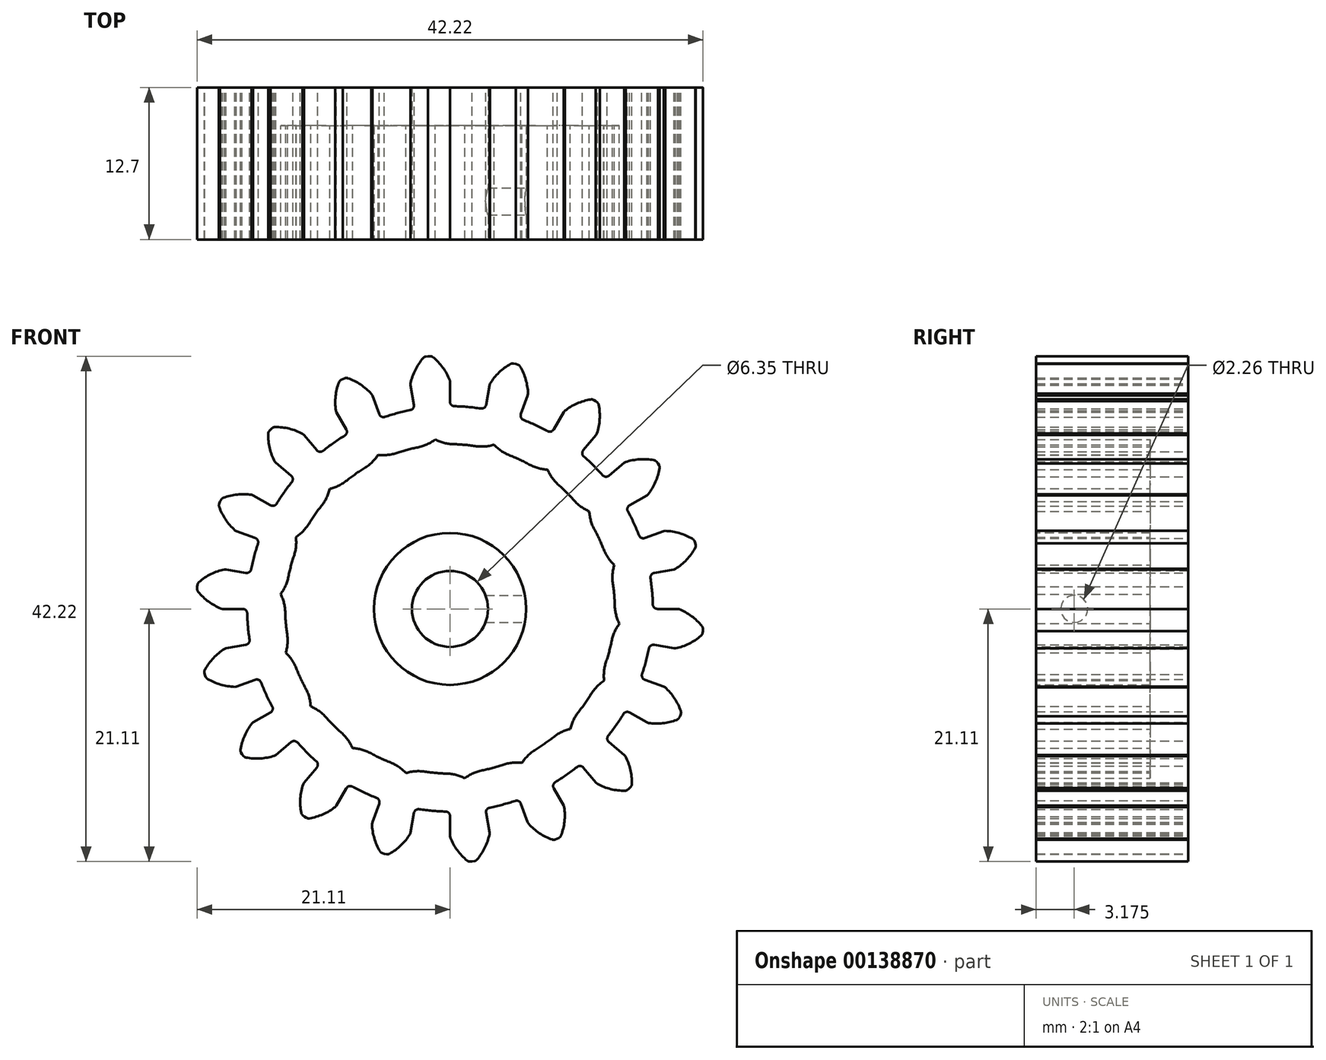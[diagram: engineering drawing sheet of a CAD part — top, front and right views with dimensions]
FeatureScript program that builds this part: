
annotation { "Feature Type Name" : "Feature", "Feature Type Description" : "" }
export const myFeature = defineFeature(function(context is Context, id is Id, definition is map)
    precondition{}
    {
        {
            var Q0;
            Q0=qCreatedBy(makeId("Front.planeOp"),FACE);
            var sketch = newSketch(context, id + "F0", { "sketchPlane" : qUnion([Q0])});
            skArc(sketch, "E0", {"start": v(-3.3, 16.6) * mm, "mid": v(-4.38, 16.36) * mm, "end": v(-5.44, 16.04) * mm});
            skArc(sketch, "E1.trimOffspring", {"start": v(-0.03, 19.12) * mm, "mid": v(-0.6, 20.16) * mm, "end": v(-1.43, 21.02) * mm});
            skLineSegment(sketch, "E2", {"start": v(-1.67, 21.11) * mm, "end": v(-1.85, 21.11) * mm});
            skLineSegment(sketch, "E3", {"start": v(0, 18.98) * mm, "end": v(0, 17.31) * mm});
            skLineSegment(sketch, "E4.MirrorCS", {"start": v(-2.02, 21.08) * mm, "end": v(-1.85, 21.11) * mm});
            skArc(sketch, "E5.MirrorCS", {"start": v(-3.3, 18.83) * mm, "mid": v(-2.9, 19.96) * mm, "end": v(-2.25, 20.95) * mm});
            skLineSegment(sketch, "E6.MirrorCS", {"start": v(-3.3, 18.69) * mm, "end": v(-3, 17.05) * mm});
            skPoint(sketch, "E7.visualSharp", {"position": v(-3.3, 18.76) * mm});
            skArc(sketch, "E7.filletArc", {"start": v(-3.3, 18.83) * mm, "mid": v(-3.3, 18.76) * mm, "end": v(-3.3, 18.69) * mm});
            skPoint(sketch, "E8.visualSharp", {"position": v(0, 19.05) * mm});
            skArc(sketch, "E8.filletArc", {"start": v(0, 18.98) * mm, "mid": v(0, 19.05) * mm, "end": v(-0.03, 19.12) * mm});
            skPoint(sketch, "E9.visualSharp", {"position": v(-2.94, 16.68) * mm});
            skArc(sketch, "E9.filletArc", {"start": v(-3.3, 16.6) * mm, "mid": v(-3.07, 16.77) * mm, "end": v(-3, 17.05) * mm});
            skPoint(sketch, "E10.visualSharp", {"position": v(0, 16.93) * mm});
            skArc(sketch, "E10.filletArc", {"start": v(0, 17.31) * mm, "mid": v(0.1, 17.04) * mm, "end": v(0.37, 16.93) * mm});
            skPoint(sketch, "E11.visualSharp", {"position": v(-2.15, 21.06) * mm});
            skArc(sketch, "E11.filletArc", {"start": v(-2.02, 21.08) * mm, "mid": v(-2.15, 21.04) * mm, "end": v(-2.25, 20.95) * mm});
            skPoint(sketch, "E12.visualSharp", {"position": v(-1.54, 21.11) * mm});
            skArc(sketch, "E12.filletArc", {"start": v(-1.43, 21.02) * mm, "mid": v(-1.54, 21.09) * mm, "end": v(-1.67, 21.11) * mm});
            skArc(sketch, "E13.1.0", {"start": v(-9.54, 16.57) * mm, "mid": v(-9.55, 17.76) * mm, "end": v(-9.28, 18.92) * mm});
            skLineSegment(sketch, "E13.1.1", {"start": v(-9.49, 16.44) * mm, "end": v(-8.66, 15) * mm});
            skArc(sketch, "E13.1.2", {"start": v(-8.79, 14.47) * mm, "mid": v(-8.62, 14.7) * mm, "end": v(-8.66, 15) * mm});
            skLineSegment(sketch, "E13.1.3", {"start": v(-9.11, 19.12) * mm, "end": v(-8.96, 19.2) * mm});
            skLineSegment(sketch, "E13.1.4", {"start": v(-8.79, 19.27) * mm, "end": v(-8.96, 19.2) * mm});
            skArc(sketch, "E13.1.5", {"start": v(-8.53, 19.27) * mm, "mid": v(-8.66, 19.3) * mm, "end": v(-8.79, 19.27) * mm});
            skArc(sketch, "E13.1.6", {"start": v(-9.11, 19.12) * mm, "mid": v(-9.21, 19.03) * mm, "end": v(-9.28, 18.92) * mm});
            skArc(sketch, "E13.1.7", {"start": v(-6.57, 17.96) * mm, "mid": v(-7.47, 18.74) * mm, "end": v(-8.53, 19.27) * mm});
            skLineSegment(sketch, "E13.1.8", {"start": v(-6.5, 17.83) * mm, "end": v(-5.92, 16.27) * mm});
            skArc(sketch, "E13.1.9", {"start": v(-5.92, 16.27) * mm, "mid": v(-5.73, 16.05) * mm, "end": v(-5.44, 16.04) * mm});
            skPoint(sketch, "E13.1.10", {"position": v(-6.52, 17.9) * mm});
            skPoint(sketch, "E13.1.11", {"position": v(-9.53, 16.5) * mm});
            skArc(sketch, "E13.2.0", {"start": v(-14.63, 12.31) * mm, "mid": v(-15.05, 13.42) * mm, "end": v(-15.19, 14.6) * mm});
            skLineSegment(sketch, "E13.2.1", {"start": v(-14.54, 12.2) * mm, "end": v(-13.26, 11.13) * mm});
            skArc(sketch, "E13.2.2", {"start": v(-13.2, 10.6) * mm, "mid": v(-13.13, 10.87) * mm, "end": v(-13.26, 11.13) * mm});
            skLineSegment(sketch, "E13.2.3", {"start": v(-15.1, 14.85) * mm, "end": v(-14.98, 14.98) * mm});
            skLineSegment(sketch, "E13.2.4", {"start": v(-14.85, 15.1) * mm, "end": v(-14.98, 14.98) * mm});
            skArc(sketch, "E13.2.5", {"start": v(-14.6, 15.19) * mm, "mid": v(-14.74, 15.16) * mm, "end": v(-14.85, 15.1) * mm});
            skArc(sketch, "E13.2.6", {"start": v(-15.1, 14.85) * mm, "mid": v(-15.16, 14.74) * mm, "end": v(-15.19, 14.6) * mm});
            skArc(sketch, "E13.2.7", {"start": v(-12.31, 14.63) * mm, "mid": v(-13.42, 15.05) * mm, "end": v(-14.6, 15.19) * mm});
            skLineSegment(sketch, "E13.2.8", {"start": v(-12.2, 14.54) * mm, "end": v(-11.13, 13.26) * mm});
            skArc(sketch, "E13.2.9", {"start": v(-11.13, 13.26) * mm, "mid": v(-10.87, 13.13) * mm, "end": v(-10.6, 13.2) * mm});
            skPoint(sketch, "E13.2.10", {"position": v(-12.25, 14.6) * mm});
            skPoint(sketch, "E13.2.11", {"position": v(-14.6, 12.25) * mm});
            skArc(sketch, "E13.3.0", {"start": v(-17.96, 6.57) * mm, "mid": v(-18.74, 7.47) * mm, "end": v(-19.27, 8.53) * mm});
            skLineSegment(sketch, "E13.3.1", {"start": v(-17.83, 6.5) * mm, "end": v(-16.27, 5.92) * mm});
            skArc(sketch, "E13.3.2", {"start": v(-16.04, 5.44) * mm, "mid": v(-16.05, 5.73) * mm, "end": v(-16.27, 5.92) * mm});
            skLineSegment(sketch, "E13.3.3", {"start": v(-19.27, 8.79) * mm, "end": v(-19.2, 8.96) * mm});
            skLineSegment(sketch, "E13.3.4", {"start": v(-19.12, 9.11) * mm, "end": v(-19.2, 8.96) * mm});
            skArc(sketch, "E13.3.5", {"start": v(-18.92, 9.28) * mm, "mid": v(-19.03, 9.21) * mm, "end": v(-19.12, 9.11) * mm});
            skArc(sketch, "E13.3.6", {"start": v(-19.27, 8.79) * mm, "mid": v(-19.3, 8.66) * mm, "end": v(-19.27, 8.53) * mm});
            skArc(sketch, "E13.3.7", {"start": v(-16.57, 9.54) * mm, "mid": v(-17.76, 9.55) * mm, "end": v(-18.92, 9.28) * mm});
            skLineSegment(sketch, "E13.3.8", {"start": v(-16.44, 9.49) * mm, "end": v(-15, 8.66) * mm});
            skArc(sketch, "E13.3.9", {"start": v(-15, 8.66) * mm, "mid": v(-14.7, 8.62) * mm, "end": v(-14.47, 8.79) * mm});
            skPoint(sketch, "E13.3.10", {"position": v(-16.5, 9.53) * mm});
            skPoint(sketch, "E13.3.11", {"position": v(-17.9, 6.52) * mm});
            skArc(sketch, "E13.4.0", {"start": v(-19.12, 0.03) * mm, "mid": v(-20.16, 0.6) * mm, "end": v(-21.02, 1.43) * mm});
            skLineSegment(sketch, "E13.4.1", {"start": v(-18.98, 0) * mm, "end": v(-17.31, 0) * mm});
            skArc(sketch, "E13.4.2", {"start": v(-16.93, -0.37) * mm, "mid": v(-17.04, -0.1) * mm, "end": v(-17.31, 0) * mm});
            skLineSegment(sketch, "E13.4.3", {"start": v(-21.11, 1.67) * mm, "end": v(-21.11, 1.85) * mm});
            skLineSegment(sketch, "E13.4.4", {"start": v(-21.08, 2.02) * mm, "end": v(-21.11, 1.85) * mm});
            skArc(sketch, "E13.4.5", {"start": v(-20.95, 2.25) * mm, "mid": v(-21.04, 2.15) * mm, "end": v(-21.08, 2.02) * mm});
            skArc(sketch, "E13.4.6", {"start": v(-21.11, 1.67) * mm, "mid": v(-21.09, 1.54) * mm, "end": v(-21.02, 1.43) * mm});
            skArc(sketch, "E13.4.7", {"start": v(-18.83, 3.3) * mm, "mid": v(-19.96, 2.9) * mm, "end": v(-20.95, 2.25) * mm});
            skLineSegment(sketch, "E13.4.8", {"start": v(-18.69, 3.3) * mm, "end": v(-17.05, 3) * mm});
            skArc(sketch, "E13.4.9", {"start": v(-17.05, 3) * mm, "mid": v(-16.77, 3.07) * mm, "end": v(-16.6, 3.3) * mm});
            skPoint(sketch, "E13.4.10", {"position": v(-18.76, 3.3) * mm});
            skPoint(sketch, "E13.4.11", {"position": v(-19.05, 0) * mm});
            skArc(sketch, "E13.5.0", {"start": v(-17.98, -6.51) * mm, "mid": v(-19.15, -6.32) * mm, "end": v(-20.24, -5.85) * mm});
            skLineSegment(sketch, "E13.5.1", {"start": v(-17.83, -6.5) * mm, "end": v(-16.27, -5.92) * mm});
            skArc(sketch, "E13.5.2", {"start": v(-15.78, -6.14) * mm, "mid": v(-15.98, -5.93) * mm, "end": v(-16.27, -5.92) * mm});
            skLineSegment(sketch, "E13.5.3", {"start": v(-20.4, -5.65) * mm, "end": v(-20.47, -5.48) * mm});
            skLineSegment(sketch, "E13.5.4", {"start": v(-20.5, -5.3) * mm, "end": v(-20.47, -5.48) * mm});
            skArc(sketch, "E13.5.5", {"start": v(-20.46, -5.06) * mm, "mid": v(-20.5, -5.18) * mm, "end": v(-20.5, -5.3) * mm});
            skArc(sketch, "E13.5.6", {"start": v(-20.4, -5.65) * mm, "mid": v(-20.34, -5.77) * mm, "end": v(-20.24, -5.85) * mm});
            skArc(sketch, "E13.5.7", {"start": v(-18.82, -3.35) * mm, "mid": v(-19.75, -4.1) * mm, "end": v(-20.46, -5.06) * mm});
            skLineSegment(sketch, "E13.5.8", {"start": v(-18.69, -3.3) * mm, "end": v(-17.05, -3) * mm});
            skArc(sketch, "E13.5.9", {"start": v(-17.05, -3) * mm, "mid": v(-16.8, -2.85) * mm, "end": v(-16.74, -2.57) * mm});
            skPoint(sketch, "E13.5.10", {"position": v(-18.76, -3.3) * mm});
            skPoint(sketch, "E13.5.11", {"position": v(-17.9, -6.52) * mm});
            skArc(sketch, "E13.6.0", {"start": v(-14.66, -12.27) * mm, "mid": v(-15.83, -12.5) * mm, "end": v(-17.02, -12.42) * mm});
            skLineSegment(sketch, "E13.6.1", {"start": v(-14.54, -12.2) * mm, "end": v(-13.26, -11.13) * mm});
            skArc(sketch, "E13.6.2", {"start": v(-12.73, -11.17) * mm, "mid": v(-12.99, -11.04) * mm, "end": v(-13.26, -11.13) * mm});
            skLineSegment(sketch, "E13.6.3", {"start": v(-17.24, -12.3) * mm, "end": v(-17.36, -12.15) * mm});
            skLineSegment(sketch, "E13.6.4", {"start": v(-17.45, -12) * mm, "end": v(-17.36, -12.15) * mm});
            skArc(sketch, "E13.6.5", {"start": v(-17.5, -11.75) * mm, "mid": v(-17.5, -11.88) * mm, "end": v(-17.45, -12) * mm});
            skArc(sketch, "E13.6.6", {"start": v(-17.24, -12.3) * mm, "mid": v(-17.14, -12.38) * mm, "end": v(-17.02, -12.42) * mm});
            skArc(sketch, "E13.6.7", {"start": v(-16.54, -9.58) * mm, "mid": v(-17.16, -10.6) * mm, "end": v(-17.5, -11.75) * mm});
            skLineSegment(sketch, "E13.6.8", {"start": v(-16.44, -9.49) * mm, "end": v(-15, -8.66) * mm});
            skArc(sketch, "E13.6.9", {"start": v(-15, -8.66) * mm, "mid": v(-14.81, -8.43) * mm, "end": v(-14.85, -8.14) * mm});
            skPoint(sketch, "E13.6.10", {"position": v(-16.5, -9.52) * mm});
            skPoint(sketch, "E13.6.11", {"position": v(-14.6, -12.25) * mm});
            skArc(sketch, "E13.7.0", {"start": v(-9.58, -16.54) * mm, "mid": v(-10.6, -17.16) * mm, "end": v(-11.75, -17.5) * mm});
            skLineSegment(sketch, "E13.7.1", {"start": v(-9.49, -16.44) * mm, "end": v(-8.66, -15) * mm});
            skArc(sketch, "E13.7.2", {"start": v(-8.14, -14.85) * mm, "mid": v(-8.43, -14.81) * mm, "end": v(-8.66, -15) * mm});
            skLineSegment(sketch, "E13.7.3", {"start": v(-12, -17.45) * mm, "end": v(-12.15, -17.36) * mm});
            skLineSegment(sketch, "E13.7.4", {"start": v(-12.3, -17.24) * mm, "end": v(-12.15, -17.36) * mm});
            skArc(sketch, "E13.7.5", {"start": v(-12.42, -17.02) * mm, "mid": v(-12.38, -17.14) * mm, "end": v(-12.3, -17.24) * mm});
            skArc(sketch, "E13.7.6", {"start": v(-12, -17.45) * mm, "mid": v(-11.88, -17.5) * mm, "end": v(-11.75, -17.5) * mm});
            skArc(sketch, "E13.7.7", {"start": v(-12.27, -14.66) * mm, "mid": v(-12.5, -15.83) * mm, "end": v(-12.42, -17.02) * mm});
            skLineSegment(sketch, "E13.7.8", {"start": v(-12.2, -14.54) * mm, "end": v(-11.13, -13.26) * mm});
            skArc(sketch, "E13.7.9", {"start": v(-11.13, -13.26) * mm, "mid": v(-11.04, -12.99) * mm, "end": v(-11.17, -12.73) * mm});
            skPoint(sketch, "E13.7.10", {"position": v(-12.25, -14.6) * mm});
            skPoint(sketch, "E13.7.11", {"position": v(-9.52, -16.5) * mm});
            skArc(sketch, "E13.8.0", {"start": v(-3.35, -18.82) * mm, "mid": v(-4.1, -19.75) * mm, "end": v(-5.06, -20.46) * mm});
            skLineSegment(sketch, "E13.8.1", {"start": v(-3.3, -18.69) * mm, "end": v(-3, -17.05) * mm});
            skArc(sketch, "E13.8.2", {"start": v(-2.57, -16.74) * mm, "mid": v(-2.85, -16.8) * mm, "end": v(-3, -17.05) * mm});
            skLineSegment(sketch, "E13.8.3", {"start": v(-5.3, -20.5) * mm, "end": v(-5.48, -20.47) * mm});
            skLineSegment(sketch, "E13.8.4", {"start": v(-5.65, -20.4) * mm, "end": v(-5.48, -20.47) * mm});
            skArc(sketch, "E13.8.5", {"start": v(-5.85, -20.24) * mm, "mid": v(-5.77, -20.34) * mm, "end": v(-5.65, -20.4) * mm});
            skArc(sketch, "E13.8.6", {"start": v(-5.3, -20.5) * mm, "mid": v(-5.18, -20.5) * mm, "end": v(-5.06, -20.46) * mm});
            skArc(sketch, "E13.8.7", {"start": v(-6.51, -17.98) * mm, "mid": v(-6.32, -19.15) * mm, "end": v(-5.85, -20.24) * mm});
            skLineSegment(sketch, "E13.8.8", {"start": v(-6.5, -17.83) * mm, "end": v(-5.92, -16.27) * mm});
            skArc(sketch, "E13.8.9", {"start": v(-5.92, -16.27) * mm, "mid": v(-5.93, -15.98) * mm, "end": v(-6.14, -15.78) * mm});
            skPoint(sketch, "E13.8.10", {"position": v(-6.52, -17.9) * mm});
            skPoint(sketch, "E13.8.11", {"position": v(-3.3, -18.76) * mm});
            skArc(sketch, "E13.9.0", {"start": v(3.3, -18.83) * mm, "mid": v(2.9, -19.96) * mm, "end": v(2.25, -20.95) * mm});
            skLineSegment(sketch, "E13.9.1", {"start": v(3.3, -18.69) * mm, "end": v(3, -17.05) * mm});
            skArc(sketch, "E13.9.2", {"start": v(3.3, -16.6) * mm, "mid": v(3.07, -16.77) * mm, "end": v(3, -17.05) * mm});
            skLineSegment(sketch, "E13.9.3", {"start": v(2.02, -21.08) * mm, "end": v(1.85, -21.11) * mm});
            skLineSegment(sketch, "E13.9.4", {"start": v(1.67, -21.11) * mm, "end": v(1.85, -21.11) * mm});
            skArc(sketch, "E13.9.5", {"start": v(1.43, -21.02) * mm, "mid": v(1.54, -21.09) * mm, "end": v(1.67, -21.11) * mm});
            skArc(sketch, "E13.9.6", {"start": v(2.02, -21.08) * mm, "mid": v(2.15, -21.04) * mm, "end": v(2.25, -20.95) * mm});
            skArc(sketch, "E13.9.7", {"start": v(0.03, -19.12) * mm, "mid": v(0.6, -20.16) * mm, "end": v(1.43, -21.02) * mm});
            skLineSegment(sketch, "E13.9.8", {"start": v(0, -18.98) * mm, "end": v(0, -17.31) * mm});
            skArc(sketch, "E13.9.9", {"start": v(0, -17.31) * mm, "mid": v(-0.1, -17.04) * mm, "end": v(-0.37, -16.93) * mm});
            skPoint(sketch, "E13.9.10", {"position": v(0, -19.05) * mm});
            skPoint(sketch, "E13.9.11", {"position": v(3.3, -18.76) * mm});
            skArc(sketch, "E13.10.0", {"start": v(9.54, -16.57) * mm, "mid": v(9.55, -17.76) * mm, "end": v(9.28, -18.92) * mm});
            skLineSegment(sketch, "E13.10.1", {"start": v(9.49, -16.44) * mm, "end": v(8.66, -15) * mm});
            skArc(sketch, "E13.10.2", {"start": v(8.79, -14.47) * mm, "mid": v(8.62, -14.7) * mm, "end": v(8.66, -15) * mm});
            skLineSegment(sketch, "E13.10.3", {"start": v(9.11, -19.12) * mm, "end": v(8.96, -19.2) * mm});
            skLineSegment(sketch, "E13.10.4", {"start": v(8.79, -19.27) * mm, "end": v(8.96, -19.2) * mm});
            skArc(sketch, "E13.10.5", {"start": v(8.53, -19.27) * mm, "mid": v(8.66, -19.3) * mm, "end": v(8.79, -19.27) * mm});
            skArc(sketch, "E13.10.6", {"start": v(9.11, -19.12) * mm, "mid": v(9.21, -19.03) * mm, "end": v(9.28, -18.92) * mm});
            skArc(sketch, "E13.10.7", {"start": v(6.57, -17.96) * mm, "mid": v(7.47, -18.74) * mm, "end": v(8.53, -19.27) * mm});
            skLineSegment(sketch, "E13.10.8", {"start": v(6.5, -17.83) * mm, "end": v(5.92, -16.27) * mm});
            skArc(sketch, "E13.10.9", {"start": v(5.92, -16.27) * mm, "mid": v(5.73, -16.05) * mm, "end": v(5.44, -16.04) * mm});
            skPoint(sketch, "E13.10.10", {"position": v(6.52, -17.9) * mm});
            skPoint(sketch, "E13.10.11", {"position": v(9.53, -16.5) * mm});
            skArc(sketch, "E13.11.0", {"start": v(14.63, -12.31) * mm, "mid": v(15.05, -13.42) * mm, "end": v(15.19, -14.6) * mm});
            skLineSegment(sketch, "E13.11.1", {"start": v(14.54, -12.2) * mm, "end": v(13.26, -11.13) * mm});
            skArc(sketch, "E13.11.2", {"start": v(13.2, -10.6) * mm, "mid": v(13.13, -10.87) * mm, "end": v(13.26, -11.13) * mm});
            skLineSegment(sketch, "E13.11.3", {"start": v(15.1, -14.85) * mm, "end": v(14.98, -14.98) * mm});
            skLineSegment(sketch, "E13.11.4", {"start": v(14.85, -15.1) * mm, "end": v(14.98, -14.98) * mm});
            skArc(sketch, "E13.11.5", {"start": v(14.6, -15.19) * mm, "mid": v(14.74, -15.16) * mm, "end": v(14.85, -15.1) * mm});
            skArc(sketch, "E13.11.6", {"start": v(15.1, -14.85) * mm, "mid": v(15.16, -14.74) * mm, "end": v(15.19, -14.6) * mm});
            skArc(sketch, "E13.11.7", {"start": v(12.31, -14.63) * mm, "mid": v(13.42, -15.05) * mm, "end": v(14.6, -15.19) * mm});
            skLineSegment(sketch, "E13.11.8", {"start": v(12.2, -14.54) * mm, "end": v(11.13, -13.26) * mm});
            skArc(sketch, "E13.11.9", {"start": v(11.13, -13.26) * mm, "mid": v(10.87, -13.13) * mm, "end": v(10.6, -13.2) * mm});
            skPoint(sketch, "E13.11.10", {"position": v(12.25, -14.6) * mm});
            skPoint(sketch, "E13.11.11", {"position": v(14.6, -12.25) * mm});
            skArc(sketch, "E13.12.0", {"start": v(17.96, -6.57) * mm, "mid": v(18.74, -7.47) * mm, "end": v(19.27, -8.53) * mm});
            skLineSegment(sketch, "E13.12.1", {"start": v(17.83, -6.5) * mm, "end": v(16.27, -5.92) * mm});
            skArc(sketch, "E13.12.2", {"start": v(16.04, -5.44) * mm, "mid": v(16.05, -5.73) * mm, "end": v(16.27, -5.92) * mm});
            skLineSegment(sketch, "E13.12.3", {"start": v(19.27, -8.79) * mm, "end": v(19.2, -8.96) * mm});
            skLineSegment(sketch, "E13.12.4", {"start": v(19.12, -9.11) * mm, "end": v(19.2, -8.96) * mm});
            skArc(sketch, "E13.12.5", {"start": v(18.92, -9.28) * mm, "mid": v(19.03, -9.21) * mm, "end": v(19.12, -9.11) * mm});
            skArc(sketch, "E13.12.6", {"start": v(19.27, -8.79) * mm, "mid": v(19.3, -8.66) * mm, "end": v(19.27, -8.53) * mm});
            skArc(sketch, "E13.12.7", {"start": v(16.57, -9.54) * mm, "mid": v(17.76, -9.55) * mm, "end": v(18.92, -9.28) * mm});
            skLineSegment(sketch, "E13.12.8", {"start": v(16.44, -9.49) * mm, "end": v(15, -8.66) * mm});
            skArc(sketch, "E13.12.9", {"start": v(15, -8.66) * mm, "mid": v(14.7, -8.62) * mm, "end": v(14.47, -8.79) * mm});
            skPoint(sketch, "E13.12.10", {"position": v(16.5, -9.53) * mm});
            skPoint(sketch, "E13.12.11", {"position": v(17.9, -6.52) * mm});
            skArc(sketch, "E13.13.0", {"start": v(19.12, -0.03) * mm, "mid": v(20.16, -0.6) * mm, "end": v(21.02, -1.43) * mm});
            skLineSegment(sketch, "E13.13.1", {"start": v(18.98, 0) * mm, "end": v(17.31, 0) * mm});
            skArc(sketch, "E13.13.2", {"start": v(16.93, 0.37) * mm, "mid": v(17.04, 0.1) * mm, "end": v(17.31, 0) * mm});
            skLineSegment(sketch, "E13.13.3", {"start": v(21.11, -1.67) * mm, "end": v(21.11, -1.85) * mm});
            skLineSegment(sketch, "E13.13.4", {"start": v(21.08, -2.02) * mm, "end": v(21.11, -1.85) * mm});
            skArc(sketch, "E13.13.5", {"start": v(20.95, -2.25) * mm, "mid": v(21.04, -2.15) * mm, "end": v(21.08, -2.02) * mm});
            skArc(sketch, "E13.13.6", {"start": v(21.11, -1.67) * mm, "mid": v(21.09, -1.54) * mm, "end": v(21.02, -1.43) * mm});
            skArc(sketch, "E13.13.7", {"start": v(18.83, -3.3) * mm, "mid": v(19.96, -2.9) * mm, "end": v(20.95, -2.25) * mm});
            skLineSegment(sketch, "E13.13.8", {"start": v(18.69, -3.3) * mm, "end": v(17.05, -3) * mm});
            skArc(sketch, "E13.13.9", {"start": v(17.05, -3) * mm, "mid": v(16.77, -3.07) * mm, "end": v(16.6, -3.3) * mm});
            skPoint(sketch, "E13.13.10", {"position": v(18.76, -3.3) * mm});
            skPoint(sketch, "E13.13.11", {"position": v(19.05, 0) * mm});
            skArc(sketch, "E13.14.0", {"start": v(17.98, 6.51) * mm, "mid": v(19.15, 6.32) * mm, "end": v(20.24, 5.85) * mm});
            skLineSegment(sketch, "E13.14.1", {"start": v(17.83, 6.5) * mm, "end": v(16.27, 5.92) * mm});
            skArc(sketch, "E13.14.2", {"start": v(15.78, 6.14) * mm, "mid": v(15.98, 5.93) * mm, "end": v(16.27, 5.92) * mm});
            skLineSegment(sketch, "E13.14.3", {"start": v(20.4, 5.65) * mm, "end": v(20.47, 5.48) * mm});
            skLineSegment(sketch, "E13.14.4", {"start": v(20.5, 5.3) * mm, "end": v(20.47, 5.48) * mm});
            skArc(sketch, "E13.14.5", {"start": v(20.46, 5.06) * mm, "mid": v(20.5, 5.18) * mm, "end": v(20.5, 5.3) * mm});
            skArc(sketch, "E13.14.6", {"start": v(20.4, 5.65) * mm, "mid": v(20.34, 5.77) * mm, "end": v(20.24, 5.85) * mm});
            skArc(sketch, "E13.14.7", {"start": v(18.82, 3.35) * mm, "mid": v(19.75, 4.1) * mm, "end": v(20.46, 5.06) * mm});
            skLineSegment(sketch, "E13.14.8", {"start": v(18.69, 3.3) * mm, "end": v(17.05, 3) * mm});
            skArc(sketch, "E13.14.9", {"start": v(17.05, 3) * mm, "mid": v(16.8, 2.85) * mm, "end": v(16.74, 2.57) * mm});
            skPoint(sketch, "E13.14.10", {"position": v(18.76, 3.3) * mm});
            skPoint(sketch, "E13.14.11", {"position": v(17.9, 6.52) * mm});
            skArc(sketch, "E13.15.0", {"start": v(14.66, 12.27) * mm, "mid": v(15.83, 12.5) * mm, "end": v(17.02, 12.42) * mm});
            skLineSegment(sketch, "E13.15.1", {"start": v(14.54, 12.2) * mm, "end": v(13.26, 11.13) * mm});
            skArc(sketch, "E13.15.2", {"start": v(12.73, 11.17) * mm, "mid": v(12.99, 11.04) * mm, "end": v(13.26, 11.13) * mm});
            skLineSegment(sketch, "E13.15.3", {"start": v(17.24, 12.3) * mm, "end": v(17.36, 12.15) * mm});
            skLineSegment(sketch, "E13.15.4", {"start": v(17.45, 12) * mm, "end": v(17.36, 12.15) * mm});
            skArc(sketch, "E13.15.5", {"start": v(17.5, 11.75) * mm, "mid": v(17.5, 11.88) * mm, "end": v(17.45, 12) * mm});
            skArc(sketch, "E13.15.6", {"start": v(17.24, 12.3) * mm, "mid": v(17.14, 12.38) * mm, "end": v(17.02, 12.42) * mm});
            skArc(sketch, "E13.15.7", {"start": v(16.54, 9.58) * mm, "mid": v(17.16, 10.6) * mm, "end": v(17.5, 11.75) * mm});
            skLineSegment(sketch, "E13.15.8", {"start": v(16.44, 9.49) * mm, "end": v(15, 8.66) * mm});
            skArc(sketch, "E13.15.9", {"start": v(15, 8.66) * mm, "mid": v(14.81, 8.43) * mm, "end": v(14.85, 8.14) * mm});
            skPoint(sketch, "E13.15.10", {"position": v(16.5, 9.52) * mm});
            skPoint(sketch, "E13.15.11", {"position": v(14.6, 12.25) * mm});
            skArc(sketch, "E13.16.0", {"start": v(9.58, 16.54) * mm, "mid": v(10.6, 17.16) * mm, "end": v(11.75, 17.5) * mm});
            skLineSegment(sketch, "E13.16.1", {"start": v(9.49, 16.44) * mm, "end": v(8.66, 15) * mm});
            skArc(sketch, "E13.16.2", {"start": v(8.14, 14.85) * mm, "mid": v(8.43, 14.81) * mm, "end": v(8.66, 15) * mm});
            skLineSegment(sketch, "E13.16.3", {"start": v(12, 17.45) * mm, "end": v(12.15, 17.36) * mm});
            skLineSegment(sketch, "E13.16.4", {"start": v(12.3, 17.24) * mm, "end": v(12.15, 17.36) * mm});
            skArc(sketch, "E13.16.5", {"start": v(12.42, 17.02) * mm, "mid": v(12.38, 17.14) * mm, "end": v(12.3, 17.24) * mm});
            skArc(sketch, "E13.16.6", {"start": v(12, 17.45) * mm, "mid": v(11.88, 17.5) * mm, "end": v(11.75, 17.5) * mm});
            skArc(sketch, "E13.16.7", {"start": v(12.27, 14.66) * mm, "mid": v(12.5, 15.83) * mm, "end": v(12.42, 17.02) * mm});
            skLineSegment(sketch, "E13.16.8", {"start": v(12.2, 14.54) * mm, "end": v(11.13, 13.26) * mm});
            skArc(sketch, "E13.16.9", {"start": v(11.13, 13.26) * mm, "mid": v(11.04, 12.99) * mm, "end": v(11.17, 12.73) * mm});
            skPoint(sketch, "E13.16.10", {"position": v(12.25, 14.6) * mm});
            skPoint(sketch, "E13.16.11", {"position": v(9.53, 16.5) * mm});
            skArc(sketch, "E13.17.0", {"start": v(3.35, 18.82) * mm, "mid": v(4.1, 19.75) * mm, "end": v(5.06, 20.46) * mm});
            skLineSegment(sketch, "E13.17.1", {"start": v(3.3, 18.69) * mm, "end": v(3, 17.05) * mm});
            skArc(sketch, "E13.17.2", {"start": v(2.57, 16.74) * mm, "mid": v(2.85, 16.8) * mm, "end": v(3, 17.05) * mm});
            skLineSegment(sketch, "E13.17.3", {"start": v(5.3, 20.5) * mm, "end": v(5.48, 20.47) * mm});
            skLineSegment(sketch, "E13.17.4", {"start": v(5.65, 20.4) * mm, "end": v(5.48, 20.47) * mm});
            skArc(sketch, "E13.17.5", {"start": v(5.85, 20.24) * mm, "mid": v(5.77, 20.34) * mm, "end": v(5.65, 20.4) * mm});
            skArc(sketch, "E13.17.6", {"start": v(5.3, 20.5) * mm, "mid": v(5.18, 20.5) * mm, "end": v(5.06, 20.46) * mm});
            skArc(sketch, "E13.17.7", {"start": v(6.51, 17.98) * mm, "mid": v(6.32, 19.15) * mm, "end": v(5.85, 20.24) * mm});
            skLineSegment(sketch, "E13.17.8", {"start": v(6.5, 17.83) * mm, "end": v(5.92, 16.27) * mm});
            skArc(sketch, "E13.17.9", {"start": v(5.92, 16.27) * mm, "mid": v(5.93, 15.98) * mm, "end": v(6.14, 15.78) * mm});
            skPoint(sketch, "E13.17.10", {"position": v(6.52, 17.9) * mm});
            skPoint(sketch, "E13.17.11", {"position": v(3.3, 18.76) * mm});
            skArc(sketch, "E14.trimOffspring", {"start": v(2.57, 16.74) * mm, "mid": v(1.48, 16.87) * mm, "end": v(0.37, 16.93) * mm});
            skArc(sketch, "E15.trimOffspring", {"start": v(8.14, 14.85) * mm, "mid": v(7.16, 15.35) * mm, "end": v(6.14, 15.78) * mm});
            skArc(sketch, "E16.trimOffspring", {"start": v(12.73, 11.17) * mm, "mid": v(11.97, 11.97) * mm, "end": v(11.17, 12.73) * mm});
            skArc(sketch, "E17.trimOffspring", {"start": v(15.78, 6.14) * mm, "mid": v(15.35, 7.16) * mm, "end": v(14.85, 8.14) * mm});
            skArc(sketch, "E18.trimOffspring", {"start": v(16.93, 0.37) * mm, "mid": v(16.87, 1.48) * mm, "end": v(16.74, 2.57) * mm});
            skArc(sketch, "E19.trimOffspring", {"start": v(16.04, -5.44) * mm, "mid": v(16.36, -4.38) * mm, "end": v(16.6, -3.3) * mm});
            skArc(sketch, "E20.trimOffspring", {"start": v(8.79, -14.47) * mm, "mid": v(9.71, -13.87) * mm, "end": v(10.6, -13.2) * mm});
            skArc(sketch, "E21.trimOffspring", {"start": v(13.2, -10.6) * mm, "mid": v(13.87, -9.71) * mm, "end": v(14.47, -8.79) * mm});
            skArc(sketch, "E22.trimOffspring", {"start": v(3.3, -16.6) * mm, "mid": v(4.38, -16.36) * mm, "end": v(5.44, -16.04) * mm});
            skArc(sketch, "E23.trimOffspring", {"start": v(-2.57, -16.74) * mm, "mid": v(-1.48, -16.87) * mm, "end": v(-0.37, -16.93) * mm});
            skArc(sketch, "E24.trimOffspring", {"start": v(-8.14, -14.85) * mm, "mid": v(-7.16, -15.35) * mm, "end": v(-6.14, -15.78) * mm});
            skArc(sketch, "E25.trimOffspring", {"start": v(-12.73, -11.17) * mm, "mid": v(-11.97, -11.97) * mm, "end": v(-11.17, -12.73) * mm});
            skArc(sketch, "E26.trimOffspring", {"start": v(-15.78, -6.14) * mm, "mid": v(-15.35, -7.16) * mm, "end": v(-14.85, -8.14) * mm});
            skArc(sketch, "E27.trimOffspring", {"start": v(-16.93, -0.37) * mm, "mid": v(-16.87, -1.48) * mm, "end": v(-16.74, -2.57) * mm});
            skArc(sketch, "E28.trimOffspring", {"start": v(-16.04, 5.44) * mm, "mid": v(-16.36, 4.38) * mm, "end": v(-16.6, 3.3) * mm});
            skArc(sketch, "E29.trimOffspring", {"start": v(-13.2, 10.6) * mm, "mid": v(-13.87, 9.71) * mm, "end": v(-14.47, 8.79) * mm});
            skArc(sketch, "E30.trimOffspring", {"start": v(-8.79, 14.47) * mm, "mid": v(-9.71, 13.87) * mm, "end": v(-10.6, 13.2) * mm});
            skLineSegment(sketch, "E31", {"start": v(-12.31, 14.63) * mm, "end": v(-12.2, 14.54) * mm});
            skLineSegment(sketch, "E32", {"start": v(-19.12, 0.03) * mm, "end": v(-18.98, 0) * mm});
            skLineSegment(sketch, "E33", {"start": v(-18.83, 3.3) * mm, "end": v(-18.69, 3.3) * mm});
            skLineSegment(sketch, "E34", {"start": v(-18.82, -3.35) * mm, "end": v(-18.69, -3.3) * mm});
            skLineSegment(sketch, "E35", {"start": v(-17.98, -6.51) * mm, "end": v(-17.83, -6.5) * mm});
            skLineSegment(sketch, "E36", {"start": v(-17.96, 6.57) * mm, "end": v(-17.83, 6.5) * mm});
            skLineSegment(sketch, "E37", {"start": v(-16.57, 9.54) * mm, "end": v(-16.44, 9.49) * mm});
            skLineSegment(sketch, "E38", {"start": v(-14.63, 12.31) * mm, "end": v(-14.54, 12.2) * mm});
            skLineSegment(sketch, "E39", {"start": v(-9.54, 16.57) * mm, "end": v(-9.49, 16.44) * mm});
            skLineSegment(sketch, "E40", {"start": v(-6.5, 17.83) * mm, "end": v(-6.57, 17.96) * mm});
            skLineSegment(sketch, "E41", {"start": v(9.49, 16.44) * mm, "end": v(9.58, 16.54) * mm});
            skLineSegment(sketch, "E42", {"start": v(12.2, 14.54) * mm, "end": v(12.27, 14.66) * mm});
            skLineSegment(sketch, "E43", {"start": v(14.54, 12.2) * mm, "end": v(14.66, 12.27) * mm});
            skLineSegment(sketch, "E44", {"start": v(16.44, 9.49) * mm, "end": v(16.54, 9.58) * mm});
            skLineSegment(sketch, "E45", {"start": v(17.83, 6.5) * mm, "end": v(17.98, 6.51) * mm});
            skLineSegment(sketch, "E46", {"start": v(18.98, 0) * mm, "end": v(19.12, -0.03) * mm});
            skLineSegment(sketch, "E47", {"start": v(18.69, 3.3) * mm, "end": v(18.82, 3.35) * mm});
            skLineSegment(sketch, "E48", {"start": v(18.69, -3.3) * mm, "end": v(18.83, -3.3) * mm});
            skLineSegment(sketch, "E49", {"start": v(16.44, -9.49) * mm, "end": v(16.57, -9.54) * mm});
            skLineSegment(sketch, "E50", {"start": v(17.83, -6.5) * mm, "end": v(17.96, -6.57) * mm});
            skLineSegment(sketch, "E51", {"start": v(14.54, -12.2) * mm, "end": v(14.63, -12.31) * mm});
            skLineSegment(sketch, "E52", {"start": v(12.31, -14.63) * mm, "end": v(12.2, -14.54) * mm});
            skLineSegment(sketch, "E53", {"start": v(9.49, -16.44) * mm, "end": v(9.54, -16.57) * mm});
            skLineSegment(sketch, "E54", {"start": v(6.5, -17.83) * mm, "end": v(6.57, -17.96) * mm});
            skLineSegment(sketch, "E55", {"start": v(3.3, -18.83) * mm, "end": v(3.3, -18.69) * mm});
            skLineSegment(sketch, "E56", {"start": v(0.03, -19.12) * mm, "end": v(0, -18.98) * mm});
            skLineSegment(sketch, "E57", {"start": v(-3.3, -18.69) * mm, "end": v(-3.35, -18.82) * mm});
            skLineSegment(sketch, "E58", {"start": v(-12.27, -14.66) * mm, "end": v(-12.2, -14.54) * mm});
            skLineSegment(sketch, "E59", {"start": v(-9.58, -16.54) * mm, "end": v(-9.49, -16.44) * mm});
            skLineSegment(sketch, "E60", {"start": v(-14.66, -12.27) * mm, "end": v(-14.54, -12.2) * mm});
            skLineSegment(sketch, "E61", {"start": v(-6.51, -17.98) * mm, "end": v(-6.5, -17.83) * mm});
            skLineSegment(sketch, "E62", {"start": v(6.51, 17.98) * mm, "end": v(6.5, 17.83) * mm});
            skLineSegment(sketch, "E63", {"start": v(3.3, 18.69) * mm, "end": v(3.35, 18.82) * mm});
            skLineSegment(sketch, "E64", {"start": v(-16.54, -9.58) * mm, "end": v(-16.44, -9.49) * mm});
            skSolve(sketch);
        }
        {
            var Q0;
            Q0 = qSketchRegion(id + "F0", true);
            extrude(context, id + "F1", {"entities" : qUnion([Q0]), "depth" : 12.7 * mm});
        }
        {
            var Q0;
            Q0=makeQuery(id+"F1.opExtrude","CAP_FACE",FACE,{"disambiguationData":[OSD([sQuery(id+"F0.wireOp",EDGE,"E0"),sQuery(id+"F0.wireOp",EDGE,"E1.trimOffspring"),sQuery(id+"F0.wireOp",EDGE,"E2"),sQuery(id+"F0.wireOp",EDGE,"E3"),sQuery(id+"F0.wireOp",EDGE,"E4.MirrorCS"),sQuery(id+"F0.wireOp",EDGE,"E5.MirrorCS"),sQuery(id+"F0.wireOp",EDGE,"E6.MirrorCS"),sQuery(id+"F0.wireOp",EDGE,"E7.filletArc"),sQuery(id+"F0.wireOp",EDGE,"E8.filletArc"),sQuery(id+"F0.wireOp",EDGE,"E9.filletArc"),sQuery(id+"F0.wireOp",EDGE,"E10.filletArc"),sQuery(id+"F0.wireOp",EDGE,"E11.filletArc"),sQuery(id+"F0.wireOp",EDGE,"E12.filletArc"),sQuery(id+"F0.wireOp",EDGE,"E13.1.0"),sQuery(id+"F0.wireOp",EDGE,"E13.1.1"),sQuery(id+"F0.wireOp",EDGE,"E13.1.2"),sQuery(id+"F0.wireOp",EDGE,"E13.1.3"),sQuery(id+"F0.wireOp",EDGE,"E13.1.4"),sQuery(id+"F0.wireOp",EDGE,"E13.1.5"),sQuery(id+"F0.wireOp",EDGE,"E13.1.6"),sQuery(id+"F0.wireOp",EDGE,"E13.1.7"),sQuery(id+"F0.wireOp",EDGE,"E13.1.8"),sQuery(id+"F0.wireOp",EDGE,"E13.1.9"),sQuery(id+"F0.wireOp",EDGE,"E13.2.0"),sQuery(id+"F0.wireOp",EDGE,"E13.2.1"),sQuery(id+"F0.wireOp",EDGE,"E13.2.2"),sQuery(id+"F0.wireOp",EDGE,"E13.2.3"),sQuery(id+"F0.wireOp",EDGE,"E13.2.4"),sQuery(id+"F0.wireOp",EDGE,"E13.2.5"),sQuery(id+"F0.wireOp",EDGE,"E13.2.6"),sQuery(id+"F0.wireOp",EDGE,"E13.2.7"),sQuery(id+"F0.wireOp",EDGE,"E13.2.8"),sQuery(id+"F0.wireOp",EDGE,"E13.2.9"),sQuery(id+"F0.wireOp",EDGE,"E13.3.0"),sQuery(id+"F0.wireOp",EDGE,"E13.3.1"),sQuery(id+"F0.wireOp",EDGE,"E13.3.2"),sQuery(id+"F0.wireOp",EDGE,"E13.3.3"),sQuery(id+"F0.wireOp",EDGE,"E13.3.4"),sQuery(id+"F0.wireOp",EDGE,"E13.3.5"),sQuery(id+"F0.wireOp",EDGE,"E13.3.6"),sQuery(id+"F0.wireOp",EDGE,"E13.3.7"),sQuery(id+"F0.wireOp",EDGE,"E13.3.8"),sQuery(id+"F0.wireOp",EDGE,"E13.3.9"),sQuery(id+"F0.wireOp",EDGE,"E13.4.0"),sQuery(id+"F0.wireOp",EDGE,"E13.4.1"),sQuery(id+"F0.wireOp",EDGE,"E13.4.2"),sQuery(id+"F0.wireOp",EDGE,"E13.4.3"),sQuery(id+"F0.wireOp",EDGE,"E13.4.4"),sQuery(id+"F0.wireOp",EDGE,"E13.4.5"),sQuery(id+"F0.wireOp",EDGE,"E13.4.6"),sQuery(id+"F0.wireOp",EDGE,"E13.4.7"),sQuery(id+"F0.wireOp",EDGE,"E13.4.8"),sQuery(id+"F0.wireOp",EDGE,"E13.4.9"),sQuery(id+"F0.wireOp",EDGE,"E13.5.0"),sQuery(id+"F0.wireOp",EDGE,"E13.5.1"),sQuery(id+"F0.wireOp",EDGE,"E13.5.2"),sQuery(id+"F0.wireOp",EDGE,"E13.5.3"),sQuery(id+"F0.wireOp",EDGE,"E13.5.4"),sQuery(id+"F0.wireOp",EDGE,"E13.5.5"),sQuery(id+"F0.wireOp",EDGE,"E13.5.6"),sQuery(id+"F0.wireOp",EDGE,"E13.5.7"),sQuery(id+"F0.wireOp",EDGE,"E13.5.8"),sQuery(id+"F0.wireOp",EDGE,"E13.5.9"),sQuery(id+"F0.wireOp",EDGE,"E13.6.0"),sQuery(id+"F0.wireOp",EDGE,"E13.6.1"),sQuery(id+"F0.wireOp",EDGE,"E13.6.2"),sQuery(id+"F0.wireOp",EDGE,"E13.6.3"),sQuery(id+"F0.wireOp",EDGE,"E13.6.4"),sQuery(id+"F0.wireOp",EDGE,"E13.6.5"),sQuery(id+"F0.wireOp",EDGE,"E13.6.6"),sQuery(id+"F0.wireOp",EDGE,"E13.6.7"),sQuery(id+"F0.wireOp",EDGE,"E13.6.8"),sQuery(id+"F0.wireOp",EDGE,"E13.6.9"),sQuery(id+"F0.wireOp",EDGE,"E13.7.0"),sQuery(id+"F0.wireOp",EDGE,"E13.7.1"),sQuery(id+"F0.wireOp",EDGE,"E13.7.2"),sQuery(id+"F0.wireOp",EDGE,"E13.7.3"),sQuery(id+"F0.wireOp",EDGE,"E13.7.4"),sQuery(id+"F0.wireOp",EDGE,"E13.7.5"),sQuery(id+"F0.wireOp",EDGE,"E13.7.6"),sQuery(id+"F0.wireOp",EDGE,"E13.7.7"),sQuery(id+"F0.wireOp",EDGE,"E13.7.8"),sQuery(id+"F0.wireOp",EDGE,"E13.7.9"),sQuery(id+"F0.wireOp",EDGE,"E13.8.0"),sQuery(id+"F0.wireOp",EDGE,"E13.8.1"),sQuery(id+"F0.wireOp",EDGE,"E13.8.2"),sQuery(id+"F0.wireOp",EDGE,"E13.8.3"),sQuery(id+"F0.wireOp",EDGE,"E13.8.4"),sQuery(id+"F0.wireOp",EDGE,"E13.8.5"),sQuery(id+"F0.wireOp",EDGE,"E13.8.6"),sQuery(id+"F0.wireOp",EDGE,"E13.8.7"),sQuery(id+"F0.wireOp",EDGE,"E13.8.8"),sQuery(id+"F0.wireOp",EDGE,"E13.8.9"),sQuery(id+"F0.wireOp",EDGE,"E13.9.0"),sQuery(id+"F0.wireOp",EDGE,"E13.9.1"),sQuery(id+"F0.wireOp",EDGE,"E13.9.2"),sQuery(id+"F0.wireOp",EDGE,"E13.9.3"),sQuery(id+"F0.wireOp",EDGE,"E13.9.4"),sQuery(id+"F0.wireOp",EDGE,"E13.9.5"),sQuery(id+"F0.wireOp",EDGE,"E13.9.6"),sQuery(id+"F0.wireOp",EDGE,"E13.9.7"),sQuery(id+"F0.wireOp",EDGE,"E13.9.8"),sQuery(id+"F0.wireOp",EDGE,"E13.9.9"),sQuery(id+"F0.wireOp",EDGE,"E13.10.0"),sQuery(id+"F0.wireOp",EDGE,"E13.10.1"),sQuery(id+"F0.wireOp",EDGE,"E13.10.2"),sQuery(id+"F0.wireOp",EDGE,"E13.10.3"),sQuery(id+"F0.wireOp",EDGE,"E13.10.4"),sQuery(id+"F0.wireOp",EDGE,"E13.10.5"),sQuery(id+"F0.wireOp",EDGE,"E13.10.6"),sQuery(id+"F0.wireOp",EDGE,"E13.10.7"),sQuery(id+"F0.wireOp",EDGE,"E13.10.8"),sQuery(id+"F0.wireOp",EDGE,"E13.10.9"),sQuery(id+"F0.wireOp",EDGE,"E13.11.0"),sQuery(id+"F0.wireOp",EDGE,"E13.11.1"),sQuery(id+"F0.wireOp",EDGE,"E13.11.2"),sQuery(id+"F0.wireOp",EDGE,"E13.11.3"),sQuery(id+"F0.wireOp",EDGE,"E13.11.4"),sQuery(id+"F0.wireOp",EDGE,"E13.11.5"),sQuery(id+"F0.wireOp",EDGE,"E13.11.6"),sQuery(id+"F0.wireOp",EDGE,"E13.11.7"),sQuery(id+"F0.wireOp",EDGE,"E13.11.8"),sQuery(id+"F0.wireOp",EDGE,"E13.11.9"),sQuery(id+"F0.wireOp",EDGE,"E13.12.0"),sQuery(id+"F0.wireOp",EDGE,"E13.12.1"),sQuery(id+"F0.wireOp",EDGE,"E13.12.2"),sQuery(id+"F0.wireOp",EDGE,"E13.12.3"),sQuery(id+"F0.wireOp",EDGE,"E13.12.4"),sQuery(id+"F0.wireOp",EDGE,"E13.12.5"),sQuery(id+"F0.wireOp",EDGE,"E13.12.6"),sQuery(id+"F0.wireOp",EDGE,"E13.12.7"),sQuery(id+"F0.wireOp",EDGE,"E13.12.8"),sQuery(id+"F0.wireOp",EDGE,"E13.12.9"),sQuery(id+"F0.wireOp",EDGE,"E13.13.0"),sQuery(id+"F0.wireOp",EDGE,"E13.13.1"),sQuery(id+"F0.wireOp",EDGE,"E13.13.2"),sQuery(id+"F0.wireOp",EDGE,"E13.13.3"),sQuery(id+"F0.wireOp",EDGE,"E13.13.4"),sQuery(id+"F0.wireOp",EDGE,"E13.13.5"),sQuery(id+"F0.wireOp",EDGE,"E13.13.6"),sQuery(id+"F0.wireOp",EDGE,"E13.13.7"),sQuery(id+"F0.wireOp",EDGE,"E13.13.8"),sQuery(id+"F0.wireOp",EDGE,"E13.13.9"),sQuery(id+"F0.wireOp",EDGE,"E13.14.0"),sQuery(id+"F0.wireOp",EDGE,"E13.14.1"),sQuery(id+"F0.wireOp",EDGE,"E13.14.2"),sQuery(id+"F0.wireOp",EDGE,"E13.14.3"),sQuery(id+"F0.wireOp",EDGE,"E13.14.4"),sQuery(id+"F0.wireOp",EDGE,"E13.14.5"),sQuery(id+"F0.wireOp",EDGE,"E13.14.6"),sQuery(id+"F0.wireOp",EDGE,"E13.14.7"),sQuery(id+"F0.wireOp",EDGE,"E13.14.8"),sQuery(id+"F0.wireOp",EDGE,"E13.14.9"),sQuery(id+"F0.wireOp",EDGE,"E13.15.0"),sQuery(id+"F0.wireOp",EDGE,"E13.15.1"),sQuery(id+"F0.wireOp",EDGE,"E13.15.2"),sQuery(id+"F0.wireOp",EDGE,"E13.15.3"),sQuery(id+"F0.wireOp",EDGE,"E13.15.4"),sQuery(id+"F0.wireOp",EDGE,"E13.15.5"),sQuery(id+"F0.wireOp",EDGE,"E13.15.6"),sQuery(id+"F0.wireOp",EDGE,"E13.15.7"),sQuery(id+"F0.wireOp",EDGE,"E13.15.8"),sQuery(id+"F0.wireOp",EDGE,"E13.15.9"),sQuery(id+"F0.wireOp",EDGE,"E13.16.0"),sQuery(id+"F0.wireOp",EDGE,"E13.16.1"),sQuery(id+"F0.wireOp",EDGE,"E13.16.2"),sQuery(id+"F0.wireOp",EDGE,"E13.16.3"),sQuery(id+"F0.wireOp",EDGE,"E13.16.4"),sQuery(id+"F0.wireOp",EDGE,"E13.16.5"),sQuery(id+"F0.wireOp",EDGE,"E13.16.6"),sQuery(id+"F0.wireOp",EDGE,"E13.16.7"),sQuery(id+"F0.wireOp",EDGE,"E13.16.8"),sQuery(id+"F0.wireOp",EDGE,"E13.16.9"),sQuery(id+"F0.wireOp",EDGE,"E13.17.0"),sQuery(id+"F0.wireOp",EDGE,"E13.17.1"),sQuery(id+"F0.wireOp",EDGE,"E13.17.2"),sQuery(id+"F0.wireOp",EDGE,"E13.17.3"),sQuery(id+"F0.wireOp",EDGE,"E13.17.4"),sQuery(id+"F0.wireOp",EDGE,"E13.17.5"),sQuery(id+"F0.wireOp",EDGE,"E13.17.6"),sQuery(id+"F0.wireOp",EDGE,"E13.17.7"),sQuery(id+"F0.wireOp",EDGE,"E13.17.8"),sQuery(id+"F0.wireOp",EDGE,"E13.17.9"),sQuery(id+"F0.wireOp",EDGE,"E14.trimOffspring"),sQuery(id+"F0.wireOp",EDGE,"E15.trimOffspring"),sQuery(id+"F0.wireOp",EDGE,"E16.trimOffspring"),sQuery(id+"F0.wireOp",EDGE,"E17.trimOffspring"),sQuery(id+"F0.wireOp",EDGE,"E18.trimOffspring"),sQuery(id+"F0.wireOp",EDGE,"E19.trimOffspring"),sQuery(id+"F0.wireOp",EDGE,"E20.trimOffspring"),sQuery(id+"F0.wireOp",EDGE,"E21.trimOffspring"),sQuery(id+"F0.wireOp",EDGE,"E22.trimOffspring"),sQuery(id+"F0.wireOp",EDGE,"E23.trimOffspring"),sQuery(id+"F0.wireOp",EDGE,"E24.trimOffspring"),sQuery(id+"F0.wireOp",EDGE,"E25.trimOffspring"),sQuery(id+"F0.wireOp",EDGE,"E26.trimOffspring"),sQuery(id+"F0.wireOp",EDGE,"E27.trimOffspring"),sQuery(id+"F0.wireOp",EDGE,"E28.trimOffspring"),sQuery(id+"F0.wireOp",EDGE,"E29.trimOffspring"),sQuery(id+"F0.wireOp",EDGE,"E30.trimOffspring"),sQuery(id+"F0.wireOp",EDGE,"E31"),sQuery(id+"F0.wireOp",EDGE,"E32"),sQuery(id+"F0.wireOp",EDGE,"E33"),sQuery(id+"F0.wireOp",EDGE,"E34"),sQuery(id+"F0.wireOp",EDGE,"E35"),sQuery(id+"F0.wireOp",EDGE,"E36"),sQuery(id+"F0.wireOp",EDGE,"E37"),sQuery(id+"F0.wireOp",EDGE,"E38"),sQuery(id+"F0.wireOp",EDGE,"E39"),sQuery(id+"F0.wireOp",EDGE,"E40"),sQuery(id+"F0.wireOp",EDGE,"E41"),sQuery(id+"F0.wireOp",EDGE,"E42"),sQuery(id+"F0.wireOp",EDGE,"E43"),sQuery(id+"F0.wireOp",EDGE,"E44"),sQuery(id+"F0.wireOp",EDGE,"E45"),sQuery(id+"F0.wireOp",EDGE,"E46"),sQuery(id+"F0.wireOp",EDGE,"E47"),sQuery(id+"F0.wireOp",EDGE,"E48"),sQuery(id+"F0.wireOp",EDGE,"E49"),sQuery(id+"F0.wireOp",EDGE,"E50"),sQuery(id+"F0.wireOp",EDGE,"E51"),sQuery(id+"F0.wireOp",EDGE,"E52"),sQuery(id+"F0.wireOp",EDGE,"E53"),sQuery(id+"F0.wireOp",EDGE,"E54"),sQuery(id+"F0.wireOp",EDGE,"E55"),sQuery(id+"F0.wireOp",EDGE,"E56"),sQuery(id+"F0.wireOp",EDGE,"E57"),sQuery(id+"F0.wireOp",EDGE,"E58"),sQuery(id+"F0.wireOp",EDGE,"E59"),sQuery(id+"F0.wireOp",EDGE,"E60"),sQuery(id+"F0.wireOp",EDGE,"E61"),sQuery(id+"F0.wireOp",EDGE,"E62"),sQuery(id+"F0.wireOp",EDGE,"E63"),sQuery(id+"F0.wireOp",EDGE,"E64")])],"isStart":false});
            var sketch = newSketch(context, id + "F2", { "sketchPlane" : qUnion([Q0])});
            skCircle(sketch, "E65", {"center": v(0, 0) * mm, "radius": 3.18 * mm});
            skSolve(sketch);
        }
        {
            var Q0;
            Q0 = qSketchRegion(id + "F2", true);
            extrude(context, id + "F3", {"entities" : qUnion([Q0]), "operationType" : NewBodyOperationType.REMOVE, "endBound" : BoundingType.THROUGH_ALL, "oppositeDirection" : true, "depth" : 25.4 * mm});
        }
        {
            var Q0;
            Q0=makeQuery(id+"F1.opExtrude","CAP_FACE",FACE,{"disambiguationData":[OSD([sQuery(id+"F0.wireOp",EDGE,"E0"),sQuery(id+"F0.wireOp",EDGE,"E1.trimOffspring"),sQuery(id+"F0.wireOp",EDGE,"E2"),sQuery(id+"F0.wireOp",EDGE,"E3"),sQuery(id+"F0.wireOp",EDGE,"E4.MirrorCS"),sQuery(id+"F0.wireOp",EDGE,"E5.MirrorCS"),sQuery(id+"F0.wireOp",EDGE,"E6.MirrorCS"),sQuery(id+"F0.wireOp",EDGE,"E7.filletArc"),sQuery(id+"F0.wireOp",EDGE,"E8.filletArc"),sQuery(id+"F0.wireOp",EDGE,"E9.filletArc"),sQuery(id+"F0.wireOp",EDGE,"E10.filletArc"),sQuery(id+"F0.wireOp",EDGE,"E11.filletArc"),sQuery(id+"F0.wireOp",EDGE,"E12.filletArc"),sQuery(id+"F0.wireOp",EDGE,"E13.1.0"),sQuery(id+"F0.wireOp",EDGE,"E13.1.1"),sQuery(id+"F0.wireOp",EDGE,"E13.1.2"),sQuery(id+"F0.wireOp",EDGE,"E13.1.3"),sQuery(id+"F0.wireOp",EDGE,"E13.1.4"),sQuery(id+"F0.wireOp",EDGE,"E13.1.5"),sQuery(id+"F0.wireOp",EDGE,"E13.1.6"),sQuery(id+"F0.wireOp",EDGE,"E13.1.7"),sQuery(id+"F0.wireOp",EDGE,"E13.1.8"),sQuery(id+"F0.wireOp",EDGE,"E13.1.9"),sQuery(id+"F0.wireOp",EDGE,"E13.2.0"),sQuery(id+"F0.wireOp",EDGE,"E13.2.1"),sQuery(id+"F0.wireOp",EDGE,"E13.2.2"),sQuery(id+"F0.wireOp",EDGE,"E13.2.3"),sQuery(id+"F0.wireOp",EDGE,"E13.2.4"),sQuery(id+"F0.wireOp",EDGE,"E13.2.5"),sQuery(id+"F0.wireOp",EDGE,"E13.2.6"),sQuery(id+"F0.wireOp",EDGE,"E13.2.7"),sQuery(id+"F0.wireOp",EDGE,"E13.2.8"),sQuery(id+"F0.wireOp",EDGE,"E13.2.9"),sQuery(id+"F0.wireOp",EDGE,"E13.3.0"),sQuery(id+"F0.wireOp",EDGE,"E13.3.1"),sQuery(id+"F0.wireOp",EDGE,"E13.3.2"),sQuery(id+"F0.wireOp",EDGE,"E13.3.3"),sQuery(id+"F0.wireOp",EDGE,"E13.3.4"),sQuery(id+"F0.wireOp",EDGE,"E13.3.5"),sQuery(id+"F0.wireOp",EDGE,"E13.3.6"),sQuery(id+"F0.wireOp",EDGE,"E13.3.7"),sQuery(id+"F0.wireOp",EDGE,"E13.3.8"),sQuery(id+"F0.wireOp",EDGE,"E13.3.9"),sQuery(id+"F0.wireOp",EDGE,"E13.4.0"),sQuery(id+"F0.wireOp",EDGE,"E13.4.1"),sQuery(id+"F0.wireOp",EDGE,"E13.4.2"),sQuery(id+"F0.wireOp",EDGE,"E13.4.3"),sQuery(id+"F0.wireOp",EDGE,"E13.4.4"),sQuery(id+"F0.wireOp",EDGE,"E13.4.5"),sQuery(id+"F0.wireOp",EDGE,"E13.4.6"),sQuery(id+"F0.wireOp",EDGE,"E13.4.7"),sQuery(id+"F0.wireOp",EDGE,"E13.4.8"),sQuery(id+"F0.wireOp",EDGE,"E13.4.9"),sQuery(id+"F0.wireOp",EDGE,"E13.5.0"),sQuery(id+"F0.wireOp",EDGE,"E13.5.1"),sQuery(id+"F0.wireOp",EDGE,"E13.5.2"),sQuery(id+"F0.wireOp",EDGE,"E13.5.3"),sQuery(id+"F0.wireOp",EDGE,"E13.5.4"),sQuery(id+"F0.wireOp",EDGE,"E13.5.5"),sQuery(id+"F0.wireOp",EDGE,"E13.5.6"),sQuery(id+"F0.wireOp",EDGE,"E13.5.7"),sQuery(id+"F0.wireOp",EDGE,"E13.5.8"),sQuery(id+"F0.wireOp",EDGE,"E13.5.9"),sQuery(id+"F0.wireOp",EDGE,"E13.6.0"),sQuery(id+"F0.wireOp",EDGE,"E13.6.1"),sQuery(id+"F0.wireOp",EDGE,"E13.6.2"),sQuery(id+"F0.wireOp",EDGE,"E13.6.3"),sQuery(id+"F0.wireOp",EDGE,"E13.6.4"),sQuery(id+"F0.wireOp",EDGE,"E13.6.5"),sQuery(id+"F0.wireOp",EDGE,"E13.6.6"),sQuery(id+"F0.wireOp",EDGE,"E13.6.7"),sQuery(id+"F0.wireOp",EDGE,"E13.6.8"),sQuery(id+"F0.wireOp",EDGE,"E13.6.9"),sQuery(id+"F0.wireOp",EDGE,"E13.7.0"),sQuery(id+"F0.wireOp",EDGE,"E13.7.1"),sQuery(id+"F0.wireOp",EDGE,"E13.7.2"),sQuery(id+"F0.wireOp",EDGE,"E13.7.3"),sQuery(id+"F0.wireOp",EDGE,"E13.7.4"),sQuery(id+"F0.wireOp",EDGE,"E13.7.5"),sQuery(id+"F0.wireOp",EDGE,"E13.7.6"),sQuery(id+"F0.wireOp",EDGE,"E13.7.7"),sQuery(id+"F0.wireOp",EDGE,"E13.7.8"),sQuery(id+"F0.wireOp",EDGE,"E13.7.9"),sQuery(id+"F0.wireOp",EDGE,"E13.8.0"),sQuery(id+"F0.wireOp",EDGE,"E13.8.1"),sQuery(id+"F0.wireOp",EDGE,"E13.8.2"),sQuery(id+"F0.wireOp",EDGE,"E13.8.3"),sQuery(id+"F0.wireOp",EDGE,"E13.8.4"),sQuery(id+"F0.wireOp",EDGE,"E13.8.5"),sQuery(id+"F0.wireOp",EDGE,"E13.8.6"),sQuery(id+"F0.wireOp",EDGE,"E13.8.7"),sQuery(id+"F0.wireOp",EDGE,"E13.8.8"),sQuery(id+"F0.wireOp",EDGE,"E13.8.9"),sQuery(id+"F0.wireOp",EDGE,"E13.9.0"),sQuery(id+"F0.wireOp",EDGE,"E13.9.1"),sQuery(id+"F0.wireOp",EDGE,"E13.9.2"),sQuery(id+"F0.wireOp",EDGE,"E13.9.3"),sQuery(id+"F0.wireOp",EDGE,"E13.9.4"),sQuery(id+"F0.wireOp",EDGE,"E13.9.5"),sQuery(id+"F0.wireOp",EDGE,"E13.9.6"),sQuery(id+"F0.wireOp",EDGE,"E13.9.7"),sQuery(id+"F0.wireOp",EDGE,"E13.9.8"),sQuery(id+"F0.wireOp",EDGE,"E13.9.9"),sQuery(id+"F0.wireOp",EDGE,"E13.10.0"),sQuery(id+"F0.wireOp",EDGE,"E13.10.1"),sQuery(id+"F0.wireOp",EDGE,"E13.10.2"),sQuery(id+"F0.wireOp",EDGE,"E13.10.3"),sQuery(id+"F0.wireOp",EDGE,"E13.10.4"),sQuery(id+"F0.wireOp",EDGE,"E13.10.5"),sQuery(id+"F0.wireOp",EDGE,"E13.10.6"),sQuery(id+"F0.wireOp",EDGE,"E13.10.7"),sQuery(id+"F0.wireOp",EDGE,"E13.10.8"),sQuery(id+"F0.wireOp",EDGE,"E13.10.9"),sQuery(id+"F0.wireOp",EDGE,"E13.11.0"),sQuery(id+"F0.wireOp",EDGE,"E13.11.1"),sQuery(id+"F0.wireOp",EDGE,"E13.11.2"),sQuery(id+"F0.wireOp",EDGE,"E13.11.3"),sQuery(id+"F0.wireOp",EDGE,"E13.11.4"),sQuery(id+"F0.wireOp",EDGE,"E13.11.5"),sQuery(id+"F0.wireOp",EDGE,"E13.11.6"),sQuery(id+"F0.wireOp",EDGE,"E13.11.7"),sQuery(id+"F0.wireOp",EDGE,"E13.11.8"),sQuery(id+"F0.wireOp",EDGE,"E13.11.9"),sQuery(id+"F0.wireOp",EDGE,"E13.12.0"),sQuery(id+"F0.wireOp",EDGE,"E13.12.1"),sQuery(id+"F0.wireOp",EDGE,"E13.12.2"),sQuery(id+"F0.wireOp",EDGE,"E13.12.3"),sQuery(id+"F0.wireOp",EDGE,"E13.12.4"),sQuery(id+"F0.wireOp",EDGE,"E13.12.5"),sQuery(id+"F0.wireOp",EDGE,"E13.12.6"),sQuery(id+"F0.wireOp",EDGE,"E13.12.7"),sQuery(id+"F0.wireOp",EDGE,"E13.12.8"),sQuery(id+"F0.wireOp",EDGE,"E13.12.9"),sQuery(id+"F0.wireOp",EDGE,"E13.13.0"),sQuery(id+"F0.wireOp",EDGE,"E13.13.1"),sQuery(id+"F0.wireOp",EDGE,"E13.13.2"),sQuery(id+"F0.wireOp",EDGE,"E13.13.3"),sQuery(id+"F0.wireOp",EDGE,"E13.13.4"),sQuery(id+"F0.wireOp",EDGE,"E13.13.5"),sQuery(id+"F0.wireOp",EDGE,"E13.13.6"),sQuery(id+"F0.wireOp",EDGE,"E13.13.7"),sQuery(id+"F0.wireOp",EDGE,"E13.13.8"),sQuery(id+"F0.wireOp",EDGE,"E13.13.9"),sQuery(id+"F0.wireOp",EDGE,"E13.14.0"),sQuery(id+"F0.wireOp",EDGE,"E13.14.1"),sQuery(id+"F0.wireOp",EDGE,"E13.14.2"),sQuery(id+"F0.wireOp",EDGE,"E13.14.3"),sQuery(id+"F0.wireOp",EDGE,"E13.14.4"),sQuery(id+"F0.wireOp",EDGE,"E13.14.5"),sQuery(id+"F0.wireOp",EDGE,"E13.14.6"),sQuery(id+"F0.wireOp",EDGE,"E13.14.7"),sQuery(id+"F0.wireOp",EDGE,"E13.14.8"),sQuery(id+"F0.wireOp",EDGE,"E13.14.9"),sQuery(id+"F0.wireOp",EDGE,"E13.15.0"),sQuery(id+"F0.wireOp",EDGE,"E13.15.1"),sQuery(id+"F0.wireOp",EDGE,"E13.15.2"),sQuery(id+"F0.wireOp",EDGE,"E13.15.3"),sQuery(id+"F0.wireOp",EDGE,"E13.15.4"),sQuery(id+"F0.wireOp",EDGE,"E13.15.5"),sQuery(id+"F0.wireOp",EDGE,"E13.15.6"),sQuery(id+"F0.wireOp",EDGE,"E13.15.7"),sQuery(id+"F0.wireOp",EDGE,"E13.15.8"),sQuery(id+"F0.wireOp",EDGE,"E13.15.9"),sQuery(id+"F0.wireOp",EDGE,"E13.16.0"),sQuery(id+"F0.wireOp",EDGE,"E13.16.1"),sQuery(id+"F0.wireOp",EDGE,"E13.16.2"),sQuery(id+"F0.wireOp",EDGE,"E13.16.3"),sQuery(id+"F0.wireOp",EDGE,"E13.16.4"),sQuery(id+"F0.wireOp",EDGE,"E13.16.5"),sQuery(id+"F0.wireOp",EDGE,"E13.16.6"),sQuery(id+"F0.wireOp",EDGE,"E13.16.7"),sQuery(id+"F0.wireOp",EDGE,"E13.16.8"),sQuery(id+"F0.wireOp",EDGE,"E13.16.9"),sQuery(id+"F0.wireOp",EDGE,"E13.17.0"),sQuery(id+"F0.wireOp",EDGE,"E13.17.1"),sQuery(id+"F0.wireOp",EDGE,"E13.17.2"),sQuery(id+"F0.wireOp",EDGE,"E13.17.3"),sQuery(id+"F0.wireOp",EDGE,"E13.17.4"),sQuery(id+"F0.wireOp",EDGE,"E13.17.5"),sQuery(id+"F0.wireOp",EDGE,"E13.17.6"),sQuery(id+"F0.wireOp",EDGE,"E13.17.7"),sQuery(id+"F0.wireOp",EDGE,"E13.17.8"),sQuery(id+"F0.wireOp",EDGE,"E13.17.9"),sQuery(id+"F0.wireOp",EDGE,"E14.trimOffspring"),sQuery(id+"F0.wireOp",EDGE,"E15.trimOffspring"),sQuery(id+"F0.wireOp",EDGE,"E16.trimOffspring"),sQuery(id+"F0.wireOp",EDGE,"E17.trimOffspring"),sQuery(id+"F0.wireOp",EDGE,"E18.trimOffspring"),sQuery(id+"F0.wireOp",EDGE,"E19.trimOffspring"),sQuery(id+"F0.wireOp",EDGE,"E20.trimOffspring"),sQuery(id+"F0.wireOp",EDGE,"E21.trimOffspring"),sQuery(id+"F0.wireOp",EDGE,"E22.trimOffspring"),sQuery(id+"F0.wireOp",EDGE,"E23.trimOffspring"),sQuery(id+"F0.wireOp",EDGE,"E24.trimOffspring"),sQuery(id+"F0.wireOp",EDGE,"E25.trimOffspring"),sQuery(id+"F0.wireOp",EDGE,"E26.trimOffspring"),sQuery(id+"F0.wireOp",EDGE,"E27.trimOffspring"),sQuery(id+"F0.wireOp",EDGE,"E28.trimOffspring"),sQuery(id+"F0.wireOp",EDGE,"E29.trimOffspring"),sQuery(id+"F0.wireOp",EDGE,"E30.trimOffspring"),sQuery(id+"F0.wireOp",EDGE,"E31"),sQuery(id+"F0.wireOp",EDGE,"E32"),sQuery(id+"F0.wireOp",EDGE,"E33"),sQuery(id+"F0.wireOp",EDGE,"E34"),sQuery(id+"F0.wireOp",EDGE,"E35"),sQuery(id+"F0.wireOp",EDGE,"E36"),sQuery(id+"F0.wireOp",EDGE,"E37"),sQuery(id+"F0.wireOp",EDGE,"E38"),sQuery(id+"F0.wireOp",EDGE,"E39"),sQuery(id+"F0.wireOp",EDGE,"E40"),sQuery(id+"F0.wireOp",EDGE,"E41"),sQuery(id+"F0.wireOp",EDGE,"E42"),sQuery(id+"F0.wireOp",EDGE,"E43"),sQuery(id+"F0.wireOp",EDGE,"E44"),sQuery(id+"F0.wireOp",EDGE,"E45"),sQuery(id+"F0.wireOp",EDGE,"E46"),sQuery(id+"F0.wireOp",EDGE,"E47"),sQuery(id+"F0.wireOp",EDGE,"E48"),sQuery(id+"F0.wireOp",EDGE,"E49"),sQuery(id+"F0.wireOp",EDGE,"E50"),sQuery(id+"F0.wireOp",EDGE,"E51"),sQuery(id+"F0.wireOp",EDGE,"E52"),sQuery(id+"F0.wireOp",EDGE,"E53"),sQuery(id+"F0.wireOp",EDGE,"E54"),sQuery(id+"F0.wireOp",EDGE,"E55"),sQuery(id+"F0.wireOp",EDGE,"E56"),sQuery(id+"F0.wireOp",EDGE,"E57"),sQuery(id+"F0.wireOp",EDGE,"E58"),sQuery(id+"F0.wireOp",EDGE,"E59"),sQuery(id+"F0.wireOp",EDGE,"E60"),sQuery(id+"F0.wireOp",EDGE,"E61"),sQuery(id+"F0.wireOp",EDGE,"E62"),sQuery(id+"F0.wireOp",EDGE,"E63"),sQuery(id+"F0.wireOp",EDGE,"E64")])],"isStart":false});
            shell(context, id + "F4", {"entities" : qUnion([Q0]), "thickness" : 3.17 * mm});
        }
        {
            var Q0;
            Q0=qCreatedBy(makeId("Right.planeOp"),FACE);
            cPlane(context, id + "F5", {"entities" : qUnion([Q0]), "cplaneType" : CPlaneType.OFFSET, "offset" : 6.35 * mm, "width" : 152.4 * mm, "height" : 152.4 * mm});
        }
        {
            var Q0;
            Q0=qCreatedBy(id+"F5.planeOp",FACE);
            var sketch = newSketch(context, id + "F6", { "sketchPlane" : qUnion([Q0])});
            skCircle(sketch, "E66", {"center": v(-9.53, 0) * mm, "radius": 1.13 * mm});
            skSolve(sketch);
        }
        {
            var Q0;
            Q0 = qSketchRegion(id + "F6", true);
            extrude(context, id + "F7", {"entities" : qUnion([Q0]), "operationType" : NewBodyOperationType.REMOVE, "oppositeDirection" : true, "depth" : 6.35 * mm});
        }
    });
